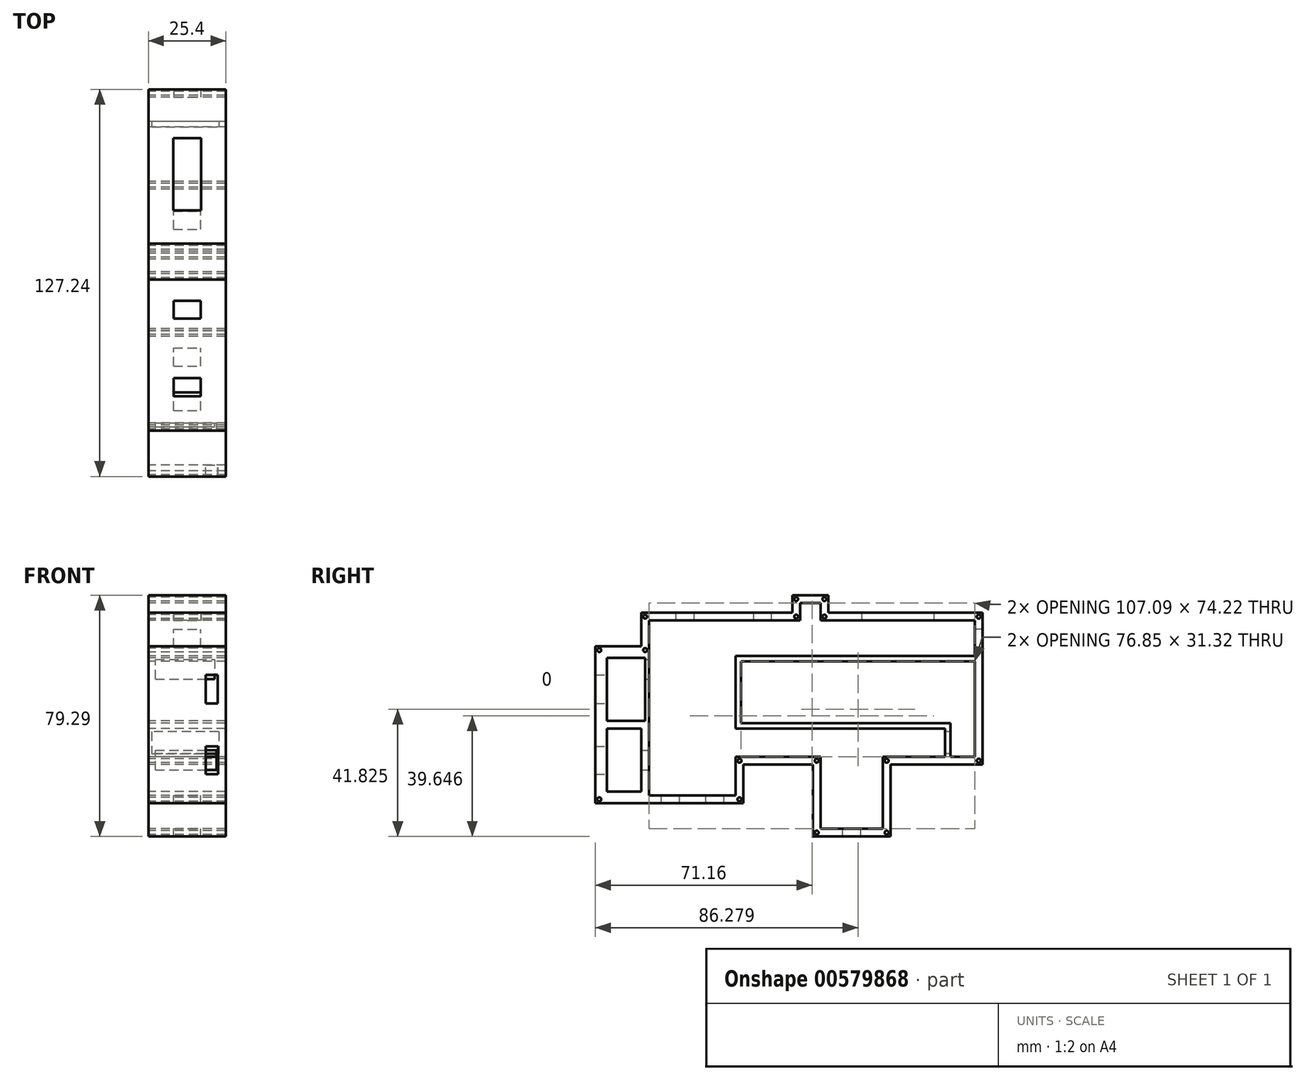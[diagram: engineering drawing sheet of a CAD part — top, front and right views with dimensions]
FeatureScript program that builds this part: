
annotation { "Feature Type Name" : "Feature", "Feature Type Description" : "" }
export const myFeature = defineFeature(function(context is Context, id is Id, definition is map)
    precondition{}
    {
        {
            var Q0;
            Q0=qCreatedBy(makeId("Right.planeOp"),FACE);
            var sketch = newSketch(context, id + "F0", { "sketchPlane" : qUnion([Q0])});
            skLineSegment(sketch, "E0", {"start": v(-47.22, 30.42) * mm, "end": v(2.39, 30.42) * mm});
            skLineSegment(sketch, "E1", {"start": v(2.39, 30.42) * mm, "end": v(2.39, 36.21) * mm});
            skLineSegment(sketch, "E2", {"start": v(2.39, 36.21) * mm, "end": v(14.22, 36.21) * mm});
            skLineSegment(sketch, "E3", {"start": v(14.22, 36.21) * mm, "end": v(14.22, 30.42) * mm});
            skLineSegment(sketch, "E4", {"start": v(14.22, 30.42) * mm, "end": v(64.94, 30.42) * mm});
            skLineSegment(sketch, "E5", {"start": v(-47.22, 30.42) * mm, "end": v(-47.22, 19.46) * mm});
            skLineSegment(sketch, "E6", {"start": v(-47.22, 19.46) * mm, "end": v(-62.3, 19.46) * mm});
            skLineSegment(sketch, "E7", {"start": v(-62.3, 19.46) * mm, "end": v(-62.3, -32.16) * mm});
            skLineSegment(sketch, "E8", {"start": v(-62.3, -32.16) * mm, "end": v(-13.68, -32.16) * mm});
            skLineSegment(sketch, "E9", {"start": v(-13.68, -32.16) * mm, "end": v(-13.68, -19.46) * mm});
            skLineSegment(sketch, "E10", {"start": v(-13.68, -19.46) * mm, "end": v(9.14, -19.46) * mm});
            skLineSegment(sketch, "E11", {"start": v(9.14, -19.46) * mm, "end": v(9.14, -43.08) * mm});
            skLineSegment(sketch, "E12", {"start": v(9.14, -43.08) * mm, "end": v(34.68, -43.08) * mm});
            skLineSegment(sketch, "E13", {"start": v(34.68, -43.08) * mm, "end": v(34.68, -19.46) * mm});
            skLineSegment(sketch, "E14", {"start": v(34.68, -19.46) * mm, "end": v(64.94, -19.46) * mm});
            skLineSegment(sketch, "E15", {"start": v(64.94, -19.46) * mm, "end": v(64.94, 30.42) * mm});
            skLineSegment(sketch, "E16", {"start": v(11.68, -19.46) * mm, "end": v(11.68, -40.54) * mm});
            skLineSegment(sketch, "E17", {"start": v(11.68, -40.54) * mm, "end": v(32.14, -40.54) * mm});
            skLineSegment(sketch, "E18", {"start": v(32.14, -40.54) * mm, "end": v(32.14, -16.92) * mm});
            skLineSegment(sketch, "E19", {"start": v(32.14, -16.92) * mm, "end": v(52.64, -16.92) * mm});
            skLineSegment(sketch, "E20", {"start": v(62.4, -16.92) * mm, "end": v(62.4, 14.4) * mm});
            skLineSegment(sketch, "E21", {"start": v(62.4, 27.88) * mm, "end": v(11.68, 27.88) * mm});
            skLineSegment(sketch, "E22", {"start": v(11.68, 27.88) * mm, "end": v(11.68, 33.67) * mm});
            skLineSegment(sketch, "E23", {"start": v(11.68, 33.67) * mm, "end": v(4.93, 33.67) * mm});
            skLineSegment(sketch, "E24", {"start": v(4.93, 33.67) * mm, "end": v(4.93, 27.88) * mm});
            skLineSegment(sketch, "E25", {"start": v(4.93, 27.88) * mm, "end": v(-44.68, 27.88) * mm});
            skLineSegment(sketch, "E26", {"start": v(-44.68, 27.88) * mm, "end": v(-44.68, 16.92) * mm});
            skLineSegment(sketch, "E27", {"start": v(-44.68, 16.92) * mm, "end": v(-59.76, 16.92) * mm});
            skLineSegment(sketch, "E28", {"start": v(-59.76, 16.92) * mm, "end": v(-59.76, -29.62) * mm});
            skLineSegment(sketch, "E29", {"start": v(-59.76, -29.62) * mm, "end": v(-16.22, -29.62) * mm});
            skLineSegment(sketch, "E30", {"start": v(-16.22, -29.62) * mm, "end": v(-16.22, -16.92) * mm});
            skLineSegment(sketch, "E31", {"start": v(-16.22, -16.92) * mm, "end": v(11.68, -16.92) * mm});
            skLineSegment(sketch, "E32", {"start": v(11.68, -16.92) * mm, "end": v(11.68, -19.46) * mm});
            skLineSegment(sketch, "E33.top", {"start": v(32.14, -43.08) * mm, "end": v(34.68, -43.08) * mm});
            skLineSegment(sketch, "E33.right", {"start": v(34.68, -40.54) * mm, "end": v(34.68, -43.08) * mm});
            skLineSegment(sketch, "E34.top", {"start": v(62.4, 30.42) * mm, "end": v(64.94, 30.42) * mm});
            skLineSegment(sketch, "E34.right", {"start": v(64.94, 27.88) * mm, "end": v(64.94, 30.42) * mm});
            skLineSegment(sketch, "E35.top", {"start": v(-44.68, 30.42) * mm, "end": v(-47.22, 30.42) * mm});
            skLineSegment(sketch, "E35.right", {"start": v(-47.22, 27.88) * mm, "end": v(-47.22, 30.42) * mm});
            skLineSegment(sketch, "E36.bottom", {"start": v(-62.3, -32.16) * mm, "end": v(-59.76, -32.16) * mm});
            skLineSegment(sketch, "E36.left", {"start": v(-62.3, -32.16) * mm, "end": v(-62.3, -29.62) * mm});
            skLineSegment(sketch, "E37.top", {"start": v(-59.76, 19.46) * mm, "end": v(-62.3, 19.46) * mm});
            skLineSegment(sketch, "E37.right", {"start": v(-62.3, 16.92) * mm, "end": v(-62.3, 19.46) * mm});
            skLineSegment(sketch, "E38.top", {"start": v(62.4, -19.46) * mm, "end": v(64.94, -19.46) * mm});
            skLineSegment(sketch, "E38.right", {"start": v(64.94, -16.92) * mm, "end": v(64.94, -19.46) * mm});
            skLineSegment(sketch, "E39.top", {"start": v(34.68, -16.92) * mm, "end": v(32.14, -16.92) * mm});
            skLineSegment(sketch, "E39.right", {"start": v(32.14, -19.46) * mm, "end": v(32.14, -16.92) * mm});
            skLineSegment(sketch, "E40.bottom", {"start": v(9.14, -43.08) * mm, "end": v(11.68, -43.08) * mm});
            skLineSegment(sketch, "E40.left", {"start": v(9.14, -43.08) * mm, "end": v(9.14, -40.54) * mm});
            skLineSegment(sketch, "E41.top", {"start": v(9.14, -16.92) * mm, "end": v(11.68, -16.92) * mm});
            skLineSegment(sketch, "E41.right", {"start": v(11.68, -19.46) * mm, "end": v(11.68, -16.92) * mm});
            skLineSegment(sketch, "E42.top", {"start": v(-13.68, -16.92) * mm, "end": v(-16.22, -16.92) * mm});
            skLineSegment(sketch, "E42.right", {"start": v(-16.22, -19.46) * mm, "end": v(-16.22, -16.92) * mm});
            skLineSegment(sketch, "E43.bottom", {"start": v(14.22, 36.21) * mm, "end": v(11.68, 36.21) * mm});
            skLineSegment(sketch, "E43.left", {"start": v(14.22, 36.21) * mm, "end": v(14.22, 33.67) * mm});
            skLineSegment(sketch, "E44.bottom", {"start": v(2.39, 36.21) * mm, "end": v(4.93, 36.21) * mm});
            skLineSegment(sketch, "E44.left", {"start": v(2.39, 36.21) * mm, "end": v(2.39, 33.67) * mm});
            skLineSegment(sketch, "E45.top", {"start": v(2.39, 27.88) * mm, "end": v(4.93, 27.88) * mm});
            skLineSegment(sketch, "E45.right", {"start": v(4.93, 30.42) * mm, "end": v(4.93, 27.88) * mm});
            skLineSegment(sketch, "E46.bottom", {"start": v(11.68, 27.88) * mm, "end": v(14.22, 27.88) * mm});
            skLineSegment(sketch, "E46.left", {"start": v(11.68, 27.88) * mm, "end": v(11.68, 30.42) * mm});
            skLineSegment(sketch, "E47.bottom", {"start": v(-13.68, -32.16) * mm, "end": v(-16.22, -32.16) * mm});
            skLineSegment(sketch, "E47.left", {"start": v(-13.68, -32.16) * mm, "end": v(-13.68, -29.62) * mm});
            skLineSegment(sketch, "E48.top", {"start": v(-47.22, 16.92) * mm, "end": v(-44.68, 16.92) * mm});
            skLineSegment(sketch, "E48.right", {"start": v(-44.68, 19.46) * mm, "end": v(-44.68, 16.92) * mm});
            skCircle(sketch, "E49", {"center": v(-61.03, 18.2) * mm, "radius": 0.65 * mm});
            skPoint(sketch, "E49.centerSnap0", {"position": v(-62.3, 18.2) * mm});
            skPoint(sketch, "E49.centerSnap1", {"position": v(-61.03, 16.92) * mm});
            skCircle(sketch, "E50", {"center": v(-45.95, 29.15) * mm, "radius": 0.64 * mm});
            skPoint(sketch, "E50.centerSnap0", {"position": v(-45.95, 27.88) * mm});
            skPoint(sketch, "E50.centerSnap1", {"position": v(-47.22, 29.15) * mm});
            skCircle(sketch, "E51", {"center": v(-45.95, 18.2) * mm, "radius": 0.65 * mm});
            skPoint(sketch, "E51.centerSnap0", {"position": v(-47.22, 18.2) * mm});
            skCircle(sketch, "E52", {"center": v(-61.03, -30.89) * mm, "radius": 0.65 * mm});
            skPoint(sketch, "E52.centerSnap0", {"position": v(-61.03, -32.16) * mm});
            skPoint(sketch, "E52.centerSnap1", {"position": v(-59.76, -30.89) * mm});
            skCircle(sketch, "E53", {"center": v(-14.95, -30.89) * mm, "radius": 0.65 * mm});
            skPoint(sketch, "E53.centerSnap0", {"position": v(-14.95, -32.16) * mm});
            skPoint(sketch, "E53.centerSnap1", {"position": v(-13.68, -30.89) * mm});
            skCircle(sketch, "E54", {"center": v(-14.95, -18.19) * mm, "radius": 0.65 * mm});
            skPoint(sketch, "E54.centerSnap0", {"position": v(-16.22, -18.19) * mm});
            skPoint(sketch, "E54.centerSnap1", {"position": v(-14.95, -19.46) * mm});
            skCircle(sketch, "E55", {"center": v(10.4, -18.19) * mm, "radius": 0.65 * mm});
            skPoint(sketch, "E55.centerSnap0", {"position": v(10.4, -19.46) * mm});
            skPoint(sketch, "E55.centerSnap1", {"position": v(11.68, -18.19) * mm});
            skCircle(sketch, "E56", {"center": v(10.4, -41.81) * mm, "radius": 0.65 * mm});
            skPoint(sketch, "E56.centerSnap0", {"position": v(10.4, -43.08) * mm});
            skPoint(sketch, "E56.centerSnap1", {"position": v(9.14, -41.81) * mm});
            skCircle(sketch, "E57", {"center": v(33.41, -41.81) * mm, "radius": 0.65 * mm});
            skPoint(sketch, "E57.centerSnap0", {"position": v(33.41, -43.08) * mm});
            skPoint(sketch, "E57.centerSnap1", {"position": v(32.14, -41.81) * mm});
            skCircle(sketch, "E58", {"center": v(33.41, -18.19) * mm, "radius": 0.65 * mm});
            skPoint(sketch, "E58.centerSnap0", {"position": v(33.41, -19.46) * mm});
            skPoint(sketch, "E58.centerSnap1", {"position": v(32.14, -18.19) * mm});
            skCircle(sketch, "E59", {"center": v(63.67, -18.19) * mm, "radius": 0.65 * mm});
            skPoint(sketch, "E59.centerSnap0", {"position": v(62.4, -18.19) * mm});
            skPoint(sketch, "E59.centerSnap1", {"position": v(63.67, -19.46) * mm});
            skCircle(sketch, "E60", {"center": v(63.67, 29.15) * mm, "radius": 0.65 * mm});
            skPoint(sketch, "E60.centerSnap0", {"position": v(63.67, 27.88) * mm});
            skPoint(sketch, "E60.centerSnap1", {"position": v(64.94, 29.15) * mm});
            skCircle(sketch, "E61", {"center": v(12.95, 29.15) * mm, "radius": 0.65 * mm});
            skPoint(sketch, "E61.centerSnap0", {"position": v(12.95, 27.88) * mm});
            skPoint(sketch, "E61.centerSnap1", {"position": v(14.22, 29.15) * mm});
            skCircle(sketch, "E62", {"center": v(12.95, 34.94) * mm, "radius": 0.65 * mm});
            skPoint(sketch, "E62.centerSnap0", {"position": v(14.22, 34.94) * mm});
            skPoint(sketch, "E62.centerSnap1", {"position": v(12.95, 33.67) * mm});
            skCircle(sketch, "E63", {"center": v(3.66, 34.94) * mm, "radius": 0.65 * mm});
            skPoint(sketch, "E63.centerSnap0", {"position": v(4.93, 34.94) * mm});
            skPoint(sketch, "E63.centerSnap1", {"position": v(3.66, 33.67) * mm});
            skCircle(sketch, "E64", {"center": v(3.66, 29.15) * mm, "radius": 0.65 * mm});
            skPoint(sketch, "E64.centerSnap0", {"position": v(4.93, 29.15) * mm});
            skPoint(sketch, "E64.centerSnap1", {"position": v(3.66, 27.88) * mm});
            skLineSegment(sketch, "E65", {"start": v(52.64, -16.92) * mm, "end": v(52.64, -7.7) * mm});
            skLineSegment(sketch, "E66", {"start": v(52.64, -7.7) * mm, "end": v(-16.22, -7.7) * mm});
            skPoint(sketch, "E67.start.orphan", {"position": v(-45.95, 16.92) * mm});
            skLineSegment(sketch, "E68", {"start": v(-14.45, 14.4) * mm, "end": v(-14.45, -5.91) * mm});
            skLineSegment(sketch, "E69", {"start": v(-14.45, -5.91) * mm, "end": v(54.42, -5.91) * mm});
            skLineSegment(sketch, "E70", {"start": v(54.42, -5.91) * mm, "end": v(54.42, -16.92) * mm});
            skLineSegment(sketch, "E71", {"start": v(-14.45, 14.4) * mm, "end": v(62.4, 14.4) * mm});
            skLineSegment(sketch, "E72", {"start": v(-16.22, -7.7) * mm, "end": v(-16.22, 16.19) * mm});
            skLineSegment(sketch, "E73", {"start": v(-16.22, 16.19) * mm, "end": v(62.4, 16.19) * mm});
            skLineSegment(sketch, "E74", {"start": v(-44.68, 16.92) * mm, "end": v(-44.68, -29.62) * mm});
            skLineSegment(sketch, "E75.bottom", {"start": v(-58.49, 15.65) * mm, "end": v(-45.95, 15.65) * mm});
            skLineSegment(sketch, "E75.top", {"start": v(-58.49, -5.08) * mm, "end": v(-45.95, -5.08) * mm});
            skLineSegment(sketch, "E75.left", {"start": v(-58.49, 15.65) * mm, "end": v(-58.49, -5.08) * mm});
            skLineSegment(sketch, "E75.right", {"start": v(-45.95, 15.65) * mm, "end": v(-45.95, -5.08) * mm});
            skLineSegment(sketch, "E76.bottom", {"start": v(-58.49, -7.62) * mm, "end": v(-47.22, -7.62) * mm});
            skLineSegment(sketch, "E76.top", {"start": v(-58.49, -28.35) * mm, "end": v(-47.22, -28.35) * mm});
            skLineSegment(sketch, "E76.left", {"start": v(-58.49, -7.62) * mm, "end": v(-58.49, -28.35) * mm});
            skLineSegment(sketch, "E76.right", {"start": v(-47.22, -7.62) * mm, "end": v(-47.22, -28.35) * mm});
            skPoint(sketch, "E77.start.orphan", {"position": v(-59.76, -6.35) * mm});
            skLineSegment(sketch, "E78.trimOffspring", {"start": v(54.42, -16.92) * mm, "end": v(62.4, -16.92) * mm});
            skLineSegment(sketch, "E79.trimOffspring", {"start": v(62.4, 16.19) * mm, "end": v(62.4, 27.88) * mm});
            skSolve(sketch);
        }
        {
            var Q0;
            Q0 = qSketchRegion(id + "F0", true);
            var Q1;
            Q1=makeQuery(id+"F0.imprint","IMPRINT",FACE,{"disambiguationData":[TD([[makeQuery(id+"F0.imprint","IMPRINT",EDGE,{"derivedFrom":sQuery(id+"F0.wireOp",EDGE,"E27")}),1.0]])]});
            extrude(context, id + "F1", {"entities" : qUnion([Q0, Q1]), "depth" : 25.4 * mm, "offsetDistance" : 25.4 * mm});
        }
        {
            var Q0;
            Q0=makeQuery(id+"F1.opExtrude","SWEPT_FACE",FACE,{"disambiguationData":[OSD([sQuery(id+"F0.wireOp",EDGE,"E65")])]});
            var sketch = newSketch(context, id + "F2", { "sketchPlane" : qUnion([Q0])});
            skLineSegment(sketch, "E80.bottom", {"start": v(1.05, -15.9) * mm, "end": v(23.12, -15.9) * mm});
            skLineSegment(sketch, "E80.top", {"start": v(1.05, -8.7) * mm, "end": v(23.12, -8.7) * mm});
            skLineSegment(sketch, "E80.left", {"start": v(1.05, -15.9) * mm, "end": v(1.05, -8.7) * mm});
            skLineSegment(sketch, "E80.right", {"start": v(23.12, -15.9) * mm, "end": v(23.12, -8.7) * mm});
            skPoint(sketch, "E80.middle", {"position": v(12.08, -12.3) * mm});
            skSolve(sketch);
        }
        {
            var Q0;
            Q0=makeQuery(id+"F1.opExtrude","SWEPT_FACE",FACE,{"disambiguationData":[OSD([sQuery(id+"F0.wireOp",EDGE,"E26"),sQuery(id+"F0.wireOp",EDGE,"E48.right"),sQuery(id+"F0.wireOp",EDGE,"E74")])]});
            var sketch = newSketch(context, id + "F3", { "sketchPlane" : qUnion([Q0])});
            skLineSegment(sketch, "E81.bottom", {"start": v(-2.24, -14.8) * mm, "end": v(-22.3, -14.8) * mm});
            skLineSegment(sketch, "E81.top", {"start": v(-2.24, -21.25) * mm, "end": v(-22.3, -21.25) * mm});
            skLineSegment(sketch, "E81.right", {"start": v(-22.3, -14.8) * mm, "end": v(-22.3, -21.25) * mm});
            skPoint(sketch, "E81.middle", {"position": v(-11.27, -18.02) * mm});
            skLineSegment(sketch, "E82.bottom", {"start": v(-2.24, 15.07) * mm, "end": v(-21.76, 15.07) * mm});
            skLineSegment(sketch, "E82.top", {"start": v(-2.24, 8.62) * mm, "end": v(-21.76, 8.62) * mm});
            skLineSegment(sketch, "E82.right", {"start": v(-21.76, 15.07) * mm, "end": v(-21.76, 8.62) * mm});
            skPoint(sketch, "E82.middle", {"position": v(-10.72, 11.84) * mm});
            skLineSegment(sketch, "E83", {"start": v(-2.24, -21.25) * mm, "end": v(-2.24, -14.8) * mm});
            skPoint(sketch, "E84.orphan", {"position": v(0.31, 15.07) * mm});
            skPoint(sketch, "E85.orphan", {"position": v(0.31, 8.62) * mm});
            skPoint(sketch, "E81.left.start.orphan", {"position": v(-0.23, -14.8) * mm});
            skPoint(sketch, "E86.orphan", {"position": v(-0.23, -21.25) * mm});
            skLineSegment(sketch, "E87.trimOffspring", {"start": v(-2.24, 8.62) * mm, "end": v(-2.24, 15.07) * mm});
            skSolve(sketch);
        }
        {
            var Q0;
            Q0=makeQuery(id+"F3.imprint","IMPRINT",FACE,{"disambiguationData":[TD([[makeQuery(id+"F3.imprint","IMPRINT",EDGE,{"derivedFrom":sQuery(id+"F3.wireOp",EDGE,"E81.bottom")}),1.0]])]});
            var Q1;
            Q1=makeQuery(id+"F3.imprint","IMPRINT",FACE,{"disambiguationData":[TD([[makeQuery(id+"F3.imprint","IMPRINT",EDGE,{"derivedFrom":sQuery(id+"F3.wireOp",EDGE,"E82.bottom")}),1.0]])]});
            extrude(context, id + "F4", {"entities" : qUnion([Q0, Q1]), "operationType" : NewBodyOperationType.REMOVE, "oppositeDirection" : true, "depth" : 10.16 * mm, "offsetDistance" : 25.4 * mm});
        }
        {
            var Q0;
            Q0=makeQuery(id+"F2.imprint","IMPRINT",FACE,{"disambiguationData":[TD([[makeQuery(id+"F2.imprint","IMPRINT",EDGE,{"derivedFrom":sQuery(id+"F2.wireOp",EDGE,"E80.bottom")}),1.0]])]});
            extrude(context, id + "F5", {"entities" : qUnion([Q0]), "operationType" : NewBodyOperationType.REMOVE, "oppositeDirection" : true, "depth" : 7.62 * mm, "offsetDistance" : 25.4 * mm});
        }
        {
            var Q0;
            Q0=makeQuery(id+"F1.opExtrude","SWEPT_FACE",FACE,{"disambiguationData":[OSD([sQuery(id+"F0.wireOp",EDGE,"E79.trimOffspring")])]});
            var sketch = newSketch(context, id + "F6", { "sketchPlane" : qUnion([Q0])});
            skLineSegment(sketch, "E88.bottom", {"start": v(8.23, 19.1) * mm, "end": v(17.17, 19.1) * mm});
            skLineSegment(sketch, "E88.top", {"start": v(8.23, 24.97) * mm, "end": v(17.17, 24.97) * mm});
            skLineSegment(sketch, "E88.left", {"start": v(8.23, 19.1) * mm, "end": v(8.23, 24.97) * mm});
            skLineSegment(sketch, "E88.right", {"start": v(17.17, 19.1) * mm, "end": v(17.17, 24.97) * mm});
            skPoint(sketch, "E88.middle", {"position": v(12.7, 22.03) * mm});
            skSolve(sketch);
        }
        {
            var Q0;
            Q0=makeQuery(id+"F1.opExtrude","SWEPT_FACE",FACE,{"disambiguationData":[OSD([sQuery(id+"F0.wireOp",EDGE,"E25"),sQuery(id+"F0.wireOp",EDGE,"E45.top")])]});
            var sketch = newSketch(context, id + "F7", { "sketchPlane" : qUnion([Q0])});
            skLineSegment(sketch, "E89.bottom", {"start": v(8.23, 30.01) * mm, "end": v(17.17, 30.01) * mm});
            skLineSegment(sketch, "E89.top", {"start": v(8.23, 35.9) * mm, "end": v(17.17, 35.9) * mm});
            skLineSegment(sketch, "E89.left", {"start": v(8.23, 30.01) * mm, "end": v(8.23, 35.9) * mm});
            skLineSegment(sketch, "E89.right", {"start": v(17.17, 30.01) * mm, "end": v(17.17, 35.9) * mm});
            skPoint(sketch, "E89.middle", {"position": v(12.7, 32.96) * mm});
            skLineSegment(sketch, "E90.bottom", {"start": v(8.23, 4.51) * mm, "end": v(17.17, 4.51) * mm});
            skLineSegment(sketch, "E90.top", {"start": v(8.23, 10.4) * mm, "end": v(17.17, 10.4) * mm});
            skLineSegment(sketch, "E90.left", {"start": v(8.23, 4.51) * mm, "end": v(8.23, 10.4) * mm});
            skLineSegment(sketch, "E90.right", {"start": v(17.17, 4.51) * mm, "end": v(17.17, 10.4) * mm});
            skPoint(sketch, "E90.middle", {"position": v(12.7, 7.46) * mm});
            skSolve(sketch);
        }
        {
            var Q0;
            Q0=makeQuery(id+"F1.opExtrude","SWEPT_FACE",FACE,{"disambiguationData":[OSD([sQuery(id+"F0.wireOp",EDGE,"E29")])]});
            var sketch = newSketch(context, id + "F8", { "sketchPlane" : qUnion([Q0])});
            skLineSegment(sketch, "E91.bottom", {"start": v(8.23, -25.98) * mm, "end": v(17.17, -25.98) * mm});
            skLineSegment(sketch, "E91.top", {"start": v(8.23, -20.09) * mm, "end": v(17.17, -20.09) * mm});
            skLineSegment(sketch, "E91.left", {"start": v(8.23, -25.98) * mm, "end": v(8.23, -20.09) * mm});
            skLineSegment(sketch, "E91.right", {"start": v(17.17, -25.98) * mm, "end": v(17.17, -20.09) * mm});
            skPoint(sketch, "E91.middle", {"position": v(12.7, -23.04) * mm});
            skLineSegment(sketch, "E92.bottom", {"start": v(8.23, -40.6) * mm, "end": v(17.17, -40.6) * mm});
            skLineSegment(sketch, "E92.top", {"start": v(8.23, -34.7) * mm, "end": v(17.17, -34.7) * mm});
            skLineSegment(sketch, "E92.left", {"start": v(8.23, -40.6) * mm, "end": v(8.23, -34.7) * mm});
            skLineSegment(sketch, "E92.right", {"start": v(17.17, -40.6) * mm, "end": v(17.17, -34.7) * mm});
            skPoint(sketch, "E92.middle", {"position": v(12.7, -37.64) * mm});
            skSolve(sketch);
        }
        {
            var Q0;
            Q0=makeQuery(id+"F1.opExtrude","SWEPT_FACE",FACE,{"disambiguationData":[OSD([sQuery(id+"F0.wireOp",EDGE,"E21"),sQuery(id+"F0.wireOp",EDGE,"E46.bottom")])]});
            var sketch = newSketch(context, id + "F9", { "sketchPlane" : qUnion([Q0])});
            skLineSegment(sketch, "E93.bottom", {"start": v(17.24, -48.88) * mm, "end": v(8.16, -48.88) * mm});
            skLineSegment(sketch, "E93.top", {"start": v(17.24, -25.2) * mm, "end": v(8.16, -25.2) * mm});
            skLineSegment(sketch, "E93.left", {"start": v(17.24, -48.88) * mm, "end": v(17.24, -25.2) * mm});
            skLineSegment(sketch, "E93.right", {"start": v(8.16, -48.88) * mm, "end": v(8.16, -25.2) * mm});
            skPoint(sketch, "E93.middle", {"position": v(12.7, -37.04) * mm});
            skSolve(sketch);
        }
        {
            var Q0;
            Q0=makeQuery(id+"F1.opExtrude","SWEPT_FACE",FACE,{"disambiguationData":[OSD([sQuery(id+"F0.wireOp",EDGE,"E17")])]});
            var sketch = newSketch(context, id + "F10", { "sketchPlane" : qUnion([Q0])});
            skLineSegment(sketch, "E94.bottom", {"start": v(8.23, 18.96) * mm, "end": v(17.17, 18.96) * mm});
            skLineSegment(sketch, "E94.top", {"start": v(8.23, 24.86) * mm, "end": v(17.17, 24.86) * mm});
            skLineSegment(sketch, "E94.left", {"start": v(8.23, 18.96) * mm, "end": v(8.23, 24.86) * mm});
            skLineSegment(sketch, "E94.right", {"start": v(17.17, 18.96) * mm, "end": v(17.17, 24.86) * mm});
            skPoint(sketch, "E94.middle", {"position": v(12.7, 21.91) * mm});
            skSolve(sketch);
        }
        {
            var Q0;
            Q0=makeQuery(id+"F1.opExtrude","SWEPT_FACE",FACE,{"disambiguationData":[OSD([sQuery(id+"F0.wireOp",EDGE,"E76.left")])]});
            var sketch = newSketch(context, id + "F11", { "sketchPlane" : qUnion([Q0])});
            skLineSegment(sketch, "E95.bottom", {"start": v(-18.81, -13.44) * mm, "end": v(-22.8, -13.44) * mm});
            skLineSegment(sketch, "E95.top", {"start": v(-18.81, -22.6) * mm, "end": v(-22.8, -22.6) * mm});
            skLineSegment(sketch, "E95.left", {"start": v(-18.81, -13.44) * mm, "end": v(-18.81, -22.6) * mm});
            skLineSegment(sketch, "E95.right", {"start": v(-22.8, -13.44) * mm, "end": v(-22.8, -22.6) * mm});
            skPoint(sketch, "E95.middle", {"position": v(-20.8, -18.02) * mm});
            skSolve(sketch);
        }
        {
            var Q0;
            Q0=makeQuery(id+"F1.opExtrude","SWEPT_FACE",FACE,{"disambiguationData":[OSD([sQuery(id+"F0.wireOp",EDGE,"E75.left")])]});
            var sketch = newSketch(context, id + "F12", { "sketchPlane" : qUnion([Q0])});
            skLineSegment(sketch, "E96.bottom", {"start": v(-18.8, 9.99) * mm, "end": v(-22.78, 9.99) * mm});
            skLineSegment(sketch, "E96.top", {"start": v(-18.8, 0.59) * mm, "end": v(-22.78, 0.59) * mm});
            skLineSegment(sketch, "E96.left", {"start": v(-18.8, 9.99) * mm, "end": v(-18.8, 0.59) * mm});
            skLineSegment(sketch, "E96.right", {"start": v(-22.78, 9.99) * mm, "end": v(-22.78, 0.59) * mm});
            skPoint(sketch, "E96.middle", {"position": v(-20.79, 5.29) * mm});
            skSolve(sketch);
        }
        {
            var Q0;
            Q0=makeQuery(id+"F11.imprint","IMPRINT",FACE,{"disambiguationData":[TD([[makeQuery(id+"F11.imprint","IMPRINT",EDGE,{"derivedFrom":sQuery(id+"F11.wireOp",EDGE,"E95.bottom")}),1.0]])]});
            var Q1;
            Q1=makeQuery(id+"F12.imprint","IMPRINT",FACE,{"disambiguationData":[TD([[makeQuery(id+"F12.imprint","IMPRINT",EDGE,{"derivedFrom":sQuery(id+"F12.wireOp",EDGE,"E96.bottom")}),1.0]])]});
            extrude(context, id + "F13", {"entities" : qUnion([Q0, Q1]), "operationType" : NewBodyOperationType.REMOVE, "oppositeDirection" : true, "depth" : 25.4 * mm, "offsetDistance" : 25.4 * mm});
        }
        {
            var Q0;
            Q0=makeQuery(id+"F7.imprint","IMPRINT",FACE,{"disambiguationData":[TD([[makeQuery(id+"F7.imprint","IMPRINT",EDGE,{"derivedFrom":sQuery(id+"F7.wireOp",EDGE,"E89.bottom")}),1.0]])]});
            var Q1;
            Q1=makeQuery(id+"F7.imprint","IMPRINT",FACE,{"disambiguationData":[TD([[makeQuery(id+"F7.imprint","IMPRINT",EDGE,{"derivedFrom":sQuery(id+"F7.wireOp",EDGE,"E90.bottom")}),1.0]])]});
            var Q2;
            Q2=makeQuery(id+"F9.imprint","IMPRINT",FACE,{"disambiguationData":[TD([[makeQuery(id+"F9.imprint","IMPRINT",EDGE,{"derivedFrom":sQuery(id+"F9.wireOp",EDGE,"E93.bottom")}),-1.0]])]});
            extrude(context, id + "F14", {"entities" : qUnion([Q0, Q1, Q2]), "operationType" : NewBodyOperationType.REMOVE, "oppositeDirection" : true, "depth" : 25.4 * mm, "offsetDistance" : 25.4 * mm});
        }
        {
            var Q0;
            Q0=makeQuery(id+"F6.imprint","IMPRINT",FACE,{"disambiguationData":[TD([[makeQuery(id+"F6.imprint","IMPRINT",EDGE,{"derivedFrom":sQuery(id+"F6.wireOp",EDGE,"E88.bottom")}),1.0]])]});
            extrude(context, id + "F15", {"entities" : qUnion([Q0]), "operationType" : NewBodyOperationType.REMOVE, "oppositeDirection" : true, "depth" : 25.4 * mm, "offsetDistance" : 25.4 * mm});
        }
        {
            var Q0;
            Q0=makeQuery(id+"F10.imprint","IMPRINT",FACE,{"disambiguationData":[TD([[makeQuery(id+"F10.imprint","IMPRINT",EDGE,{"derivedFrom":sQuery(id+"F10.wireOp",EDGE,"E94.bottom")}),1.0]])]});
            var Q1;
            Q1=makeQuery(id+"F8.imprint","IMPRINT",FACE,{"disambiguationData":[TD([[makeQuery(id+"F8.imprint","IMPRINT",EDGE,{"derivedFrom":sQuery(id+"F8.wireOp",EDGE,"E91.bottom")}),1.0]])]});
            var Q2;
            Q2=makeQuery(id+"F8.imprint","IMPRINT",FACE,{"disambiguationData":[TD([[makeQuery(id+"F8.imprint","IMPRINT",EDGE,{"derivedFrom":sQuery(id+"F8.wireOp",EDGE,"E92.bottom")}),1.0]])]});
            extrude(context, id + "F16", {"entities" : qUnion([Q0, Q1, Q2]), "operationType" : NewBodyOperationType.REMOVE, "oppositeDirection" : true, "depth" : 25.4 * mm, "offsetDistance" : 25.4 * mm});
        }
        {
            var Q0;
            Q0=makeQuery(id+"F1.opExtrude","SWEPT_BODY",BODY,{"disambiguationData":[OSD([sQuery(id+"F0.wireOp",EDGE,"E0"),sQuery(id+"F0.wireOp",EDGE,"E1"),sQuery(id+"F0.wireOp",EDGE,"E2"),sQuery(id+"F0.wireOp",EDGE,"E3"),sQuery(id+"F0.wireOp",EDGE,"E4"),sQuery(id+"F0.wireOp",EDGE,"E5"),sQuery(id+"F0.wireOp",EDGE,"E6"),sQuery(id+"F0.wireOp",EDGE,"E7"),sQuery(id+"F0.wireOp",EDGE,"E8"),sQuery(id+"F0.wireOp",EDGE,"E9"),sQuery(id+"F0.wireOp",EDGE,"E10"),sQuery(id+"F0.wireOp",EDGE,"E11"),sQuery(id+"F0.wireOp",EDGE,"E12"),sQuery(id+"F0.wireOp",EDGE,"E13"),sQuery(id+"F0.wireOp",EDGE,"E14"),sQuery(id+"F0.wireOp",EDGE,"E15"),sQuery(id+"F0.wireOp",EDGE,"E16"),sQuery(id+"F0.wireOp",EDGE,"E17"),sQuery(id+"F0.wireOp",EDGE,"E18"),sQuery(id+"F0.wireOp",EDGE,"E19"),sQuery(id+"F0.wireOp",EDGE,"E20"),sQuery(id+"F0.wireOp",EDGE,"E21"),sQuery(id+"F0.wireOp",EDGE,"E22"),sQuery(id+"F0.wireOp",EDGE,"E23"),sQuery(id+"F0.wireOp",EDGE,"E24"),sQuery(id+"F0.wireOp",EDGE,"E25"),sQuery(id+"F0.wireOp",EDGE,"E26"),sQuery(id+"F0.wireOp",EDGE,"E29"),sQuery(id+"F0.wireOp",EDGE,"E30"),sQuery(id+"F0.wireOp",EDGE,"E31"),sQuery(id+"F0.wireOp",EDGE,"E33.top"),sQuery(id+"F0.wireOp",EDGE,"E33.right"),sQuery(id+"F0.wireOp",EDGE,"E34.top"),sQuery(id+"F0.wireOp",EDGE,"E34.right"),sQuery(id+"F0.wireOp",EDGE,"E35.top"),sQuery(id+"F0.wireOp",EDGE,"E35.right"),sQuery(id+"F0.wireOp",EDGE,"E36.bottom"),sQuery(id+"F0.wireOp",EDGE,"E36.left"),sQuery(id+"F0.wireOp",EDGE,"E37.top"),sQuery(id+"F0.wireOp",EDGE,"E37.right"),sQuery(id+"F0.wireOp",EDGE,"E38.top"),sQuery(id+"F0.wireOp",EDGE,"E38.right"),sQuery(id+"F0.wireOp",EDGE,"E39.top"),sQuery(id+"F0.wireOp",EDGE,"E39.right"),sQuery(id+"F0.wireOp",EDGE,"E40.bottom"),sQuery(id+"F0.wireOp",EDGE,"E40.left"),sQuery(id+"F0.wireOp",EDGE,"E41.top"),sQuery(id+"F0.wireOp",EDGE,"E41.right"),sQuery(id+"F0.wireOp",EDGE,"E42.top"),sQuery(id+"F0.wireOp",EDGE,"E42.right"),sQuery(id+"F0.wireOp",EDGE,"E43.bottom"),sQuery(id+"F0.wireOp",EDGE,"E43.left"),sQuery(id+"F0.wireOp",EDGE,"E44.bottom"),sQuery(id+"F0.wireOp",EDGE,"E44.left"),sQuery(id+"F0.wireOp",EDGE,"E45.top"),sQuery(id+"F0.wireOp",EDGE,"E45.right"),sQuery(id+"F0.wireOp",EDGE,"E46.bottom"),sQuery(id+"F0.wireOp",EDGE,"E46.left"),sQuery(id+"F0.wireOp",EDGE,"E47.bottom"),sQuery(id+"F0.wireOp",EDGE,"E47.left"),sQuery(id+"F0.wireOp",EDGE,"E48.right"),sQuery(id+"F0.wireOp",EDGE,"E49"),sQuery(id+"F0.wireOp",EDGE,"E50"),sQuery(id+"F0.wireOp",EDGE,"E51"),sQuery(id+"F0.wireOp",EDGE,"E52"),sQuery(id+"F0.wireOp",EDGE,"E53"),sQuery(id+"F0.wireOp",EDGE,"E54"),sQuery(id+"F0.wireOp",EDGE,"E55"),sQuery(id+"F0.wireOp",EDGE,"E56"),sQuery(id+"F0.wireOp",EDGE,"E57"),sQuery(id+"F0.wireOp",EDGE,"E58"),sQuery(id+"F0.wireOp",EDGE,"E59"),sQuery(id+"F0.wireOp",EDGE,"E60"),sQuery(id+"F0.wireOp",EDGE,"E61"),sQuery(id+"F0.wireOp",EDGE,"E62"),sQuery(id+"F0.wireOp",EDGE,"E63"),sQuery(id+"F0.wireOp",EDGE,"E64"),sQuery(id+"F0.wireOp",EDGE,"E65"),sQuery(id+"F0.wireOp",EDGE,"E66"),sQuery(id+"F0.wireOp",EDGE,"E68"),sQuery(id+"F0.wireOp",EDGE,"E69"),sQuery(id+"F0.wireOp",EDGE,"E70"),sQuery(id+"F0.wireOp",EDGE,"E71"),sQuery(id+"F0.wireOp",EDGE,"E72"),sQuery(id+"F0.wireOp",EDGE,"E73"),sQuery(id+"F0.wireOp",EDGE,"E74"),sQuery(id+"F0.wireOp",EDGE,"E75.bottom"),sQuery(id+"F0.wireOp",EDGE,"E75.top"),sQuery(id+"F0.wireOp",EDGE,"E75.left"),sQuery(id+"F0.wireOp",EDGE,"E75.right"),sQuery(id+"F0.wireOp",EDGE,"E76.bottom"),sQuery(id+"F0.wireOp",EDGE,"E76.top"),sQuery(id+"F0.wireOp",EDGE,"E76.left"),sQuery(id+"F0.wireOp",EDGE,"E76.right"),sQuery(id+"F0.wireOp",EDGE,"E78.trimOffspring"),sQuery(id+"F0.wireOp",EDGE,"E79.trimOffspring")])]});
            transform(context, id + "F17", {"entities" : qUnion([Q0]), "transformType" : TransformType.TRANSLATION_3D, "dx" : 0 * mm, "dy" : 0 * mm, "dz" : 0 * mm, "makeCopy" : true});
        }
    });
